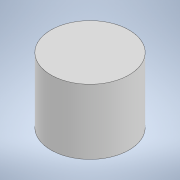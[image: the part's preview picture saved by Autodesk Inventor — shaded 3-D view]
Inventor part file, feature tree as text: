
AUTODESK INVENTOR PART (.ipt)
format: ipt  version: 2020 (Build 240168000, 168)  size: 88,064 bytes
history: native  units: mm
features: extrude x1, sketch x1
ambient origin geometry x8: Origin, YZ Plane, XZ Plane, XY Plane, X Axis, Y Axis, Z Axis, Center Point
bodies: Solid1 (feature_tree)
feature tree (2):
  extrude  "Extrusion1"  Depth=5.0mm TaperAngle=0.0deg
  sketch  "Sketch1"  dims[d0=6.0mm d1=5.0mm d2=0.0mm]
